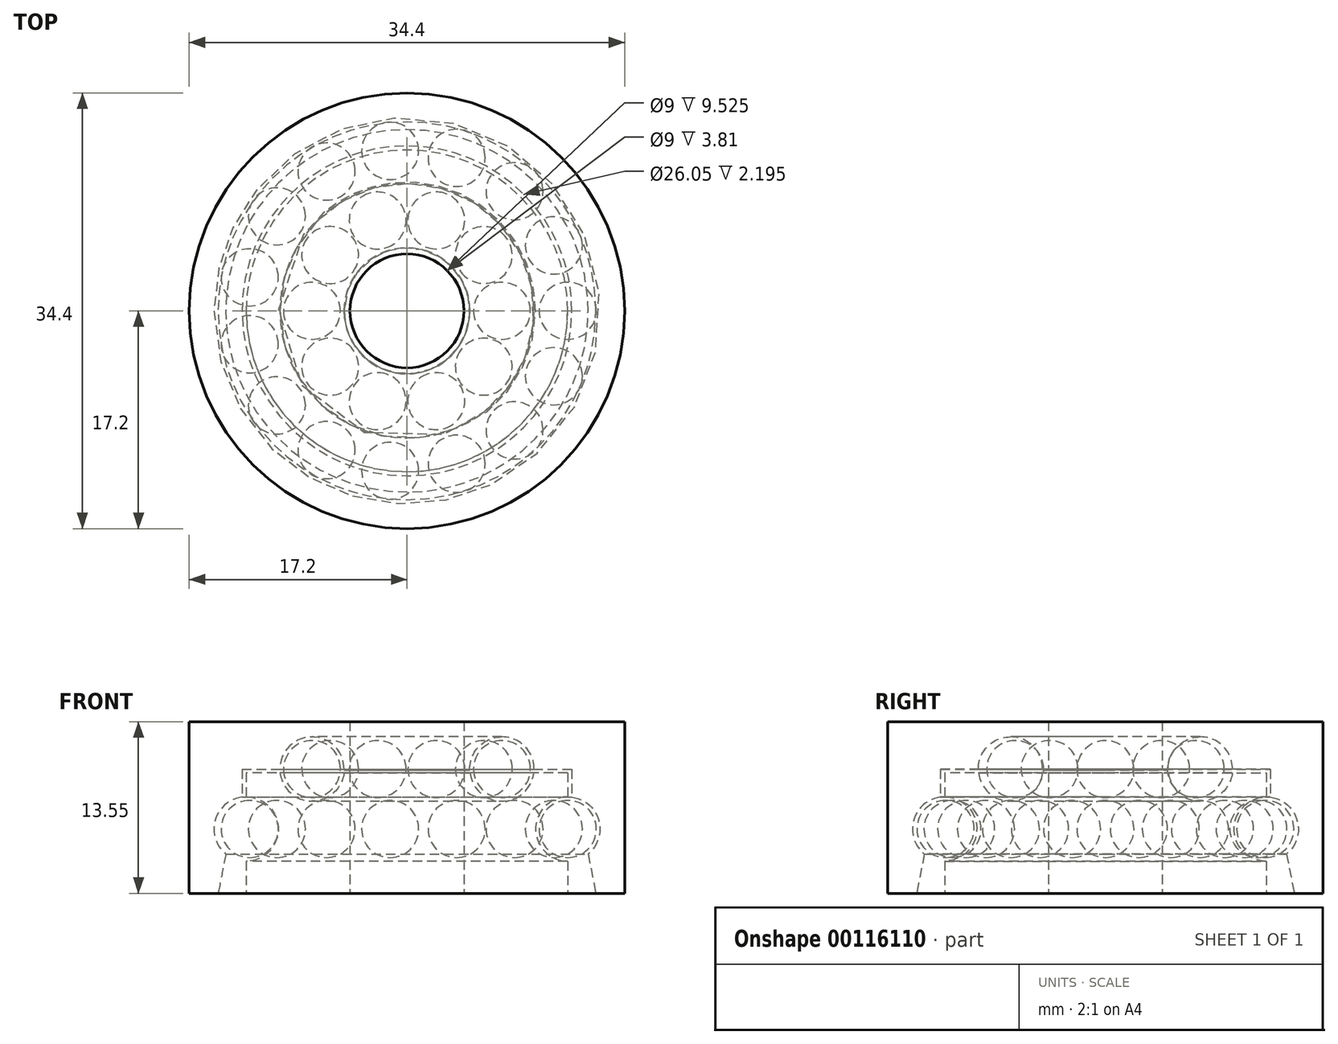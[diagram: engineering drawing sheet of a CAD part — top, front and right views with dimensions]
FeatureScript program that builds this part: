
annotation { "Feature Type Name" : "Feature", "Feature Type Description" : "" }
export const myFeature = defineFeature(function(context is Context, id is Id, definition is map)
    precondition{}
    {
        {
            var Q0;
            Q0=qCreatedBy(makeId("Top.planeOp"),FACE);
            var sketch = newSketch(context, id + "F0", { "sketchPlane" : qUnion([Q0])});
            skCircle(sketch, "E0", {"center": v(0, 0) * mm, "radius": 4.5 * mm});
            skCircle(sketch, "E1", {"center": v(0, 0) * mm, "radius": 12.7 * mm});
            skSolve(sketch);
        }
        {
            var Q0;
            Q0=makeQuery(id+"F0.imprint","IMPRINT",FACE,{"disambiguationData":[TD([[makeQuery(id+"F0.imprint","IMPRINT",EDGE,{"derivedFrom":sQuery(id+"F0.wireOp",EDGE,"E0")}),-1.0]])]});
            extrude(context, id + "F1", {"entities" : qUnion([Q0]), "depth" : 9.52 * mm});
        }
        {
            var Q0;
            Q0=qCreatedBy(makeId("Front.planeOp"),FACE);
            var sketch = newSketch(context, id + "F2", { "sketchPlane" : qUnion([Q0])});
            skCircle(sketch, "E2", {"center": v(7.5, 9.82) * mm, "radius": 2.25 * mm});
            skCircle(sketch, "E3", {"center": v(7.5, 9.82) * mm, "radius": 2.54 * mm});
            skCircle(sketch, "E4", {"center": v(12.7, 5.08) * mm, "radius": 2.26 * mm});
            skCircle(sketch, "E5", {"center": v(12.7, 5.08) * mm, "radius": 2.54 * mm});
            skLineSegment(sketch, "E6", {"start": v(5.25, 9.82) * mm, "end": v(9.75, 9.82) * mm});
            skLineSegment(sketch, "E7", {"start": v(12.7, 7.34) * mm, "end": v(12.7, 2.82) * mm});
            skSolve(sketch);
        }
        {
            var Q0;
            Q0=makeQuery(id+"F2.imprint","IMPRINT",FACE,{"disambiguationData":[TD([[makeQuery(id+"F2.imprint","IMPRINT",EDGE,{"derivedFrom":sQuery(id+"F2.wireOp",EDGE,"E2")}),-1.0]])]});
            var Q1;
            Q1=makeQuery(id+"F2.imprint","IMPRINT",FACE,{"disambiguationData":[TD([[makeQuery(id+"F2.imprint","IMPRINT",EDGE,{"derivedFrom":sQuery(id+"F2.wireOp",EDGE,"E4")}),-1.0]])]});
            var Q2;
            Q2=makeQuery(id+"F2.imprint","IMPRINT",FACE,{"disambiguationData":[TD([[makeQuery(id+"F2.imprint","IMPRINT",EDGE,{"derivedFrom":sQuery(id+"F2.wireOp",EDGE,"E4")}),1.0]])]});
            var Q3;
            Q3=makeQuery(id+"F2.imprint","IMPRINT",FACE,{"disambiguationData":[TD([[makeQuery(id+"F2.imprint","IMPRINT",EDGE,{"derivedFrom":sQuery(id+"F2.wireOp",EDGE,"E2")}),1.0]])]});
            var Q4;
            Q4=makeQuery(id+"F1.opExtrude","CAP_EDGE",EDGE,{"disambiguationData":[OSD([sQuery(id+"F0.wireOp",EDGE,"E0")])],"isStart":false});
            revolve(context, id + "F3", {"operationType" : NewBodyOperationType.REMOVE, "entities" : qUnion([Q0, Q1, Q2, Q3]), "axis" : qUnion([Q4]), "revolveType" : RevolveType.FULL, "oppositeDirection" : true});
        }
        {
            var Q0;
            Q0=qCreatedBy(makeId("Front.planeOp"),FACE);
            var sketch = newSketch(context, id + "F4", { "sketchPlane" : qUnion([Q0])});
            skCircle(sketch, "E8.0", {"center": v(12.7, 5.08) * mm, "radius": 2.54 * mm});
            skCircle(sketch, "E9.0", {"center": v(7.5, 9.82) * mm, "radius": 2.54 * mm});
            skLineSegment(sketch, "E10", {"start": v(4.96, 9.74) * mm, "end": v(4.5, 9.74) * mm});
            skLineSegment(sketch, "E11", {"start": v(4.5, 9.74) * mm, "end": v(4.5, 13.55) * mm});
            skLineSegment(sketch, "E12", {"start": v(4.5, 13.55) * mm, "end": v(17.2, 13.55) * mm});
            skLineSegment(sketch, "E13", {"start": v(17.2, 13.55) * mm, "end": v(17.2, 0) * mm});
            skLineSegment(sketch, "E14", {"start": v(17.2, 0) * mm, "end": v(14.91, 0) * mm});
            skLineSegment(sketch, "E15", {"start": v(14.91, 0) * mm, "end": v(14.3, 3.11) * mm});
            skLineSegment(sketch, "E16", {"start": v(13.03, 7.6) * mm, "end": v(13.03, 9.8) * mm});
            skLineSegment(sketch, "E17", {"start": v(13.03, 9.8) * mm, "end": v(10.04, 9.8) * mm});
            skSolve(sketch);
        }
        {
            var Q0;
            {var subQ0=sQuery(id+"F4.wireOp",EDGE,"E10");Q0=makeQuery(id+"F4.imprint","IMPRINT",FACE,{"disambiguationData":[TD([[makeQuery(id+"F4.imprint","IMPRINT",EDGE,{"derivedFrom":subQ0}),-1.0]])]});}
            var Q1;
            Q1=makeQuery(id+"F1.opExtrude","CAP_EDGE",EDGE,{"disambiguationData":[OSD([sQuery(id+"F0.wireOp",EDGE,"E1")])],"isStart":false});
            revolve(context, id + "F5", {"entities" : qUnion([Q0]), "axis" : qUnion([Q1]), "revolveType" : RevolveType.FULL});
        }
        {
            var Q0;
            {var subQ0=sQuery(id+"F2.wireOp",EDGE,"E6");Q0=makeQuery(id+"F2.imprint","IMPRINT",FACE,{"disambiguationData":[TD([[makeQuery(id+"F2.imprint","IMPRINT",EDGE,{"derivedFrom":subQ0}),1.0]])]});}
            var Q1;
            Q1=sQuery(id+"F2.wireOp",EDGE,"E6");
            revolve(context, id + "F6", {"entities" : qUnion([Q0]), "axis" : qUnion([Q1]), "revolveType" : RevolveType.FULL});
        }
        {
            var Q0;
            {var subQ0=sQuery(id+"F2.wireOp",EDGE,"E7");Q0=makeQuery(id+"F2.imprint","IMPRINT",FACE,{"disambiguationData":[TD([[makeQuery(id+"F2.imprint","IMPRINT",EDGE,{"derivedFrom":subQ0}),1.0]])]});}
            var Q1;
            Q1=sQuery(id+"F2.wireOp",EDGE,"E7");
            revolve(context, id + "F7", {"entities" : qUnion([Q0]), "axis" : qUnion([Q1]), "revolveType" : RevolveType.FULL});
        }
        {
            var Q0;
            Q0=makeQuery(id+"F6.opRevolve","SWEPT_BODY",BODY,{"disambiguationData":[OSD([sQuery(id+"F2.wireOp",EDGE,"E2"),sQuery(id+"F2.wireOp",EDGE,"E6")])]});
            var Q1;
            Q1=makeQuery(id+"F3.boolean.opBoolean","INTERSECT",EDGE,{"disambiguationData":[OD(0.0)],"derivedFrom":[makeQuery(id+"F1.opExtrude","CAP_FACE",FACE,{"disambiguationData":[OSD([sQuery(id+"F0.wireOp",EDGE,"E0"),sQuery(id+"F0.wireOp",EDGE,"E1")])],"isStart":false}),makeQuery(id+"F3.opRevolve","SWEPT_FACE",FACE,{"disambiguationData":[OSD([sQuery(id+"F2.wireOp",EDGE,"E3")])]})]});
            circularPattern(context, id + "F8", {"entities" : qUnion([Q0]), "axis" : qUnion([Q1]), "angle" : 36 * degree, "instanceCount" : 10});
        }
        {
            var Q0;
            Q0=makeQuery(id+"F7.opRevolve","SWEPT_BODY",BODY,{"disambiguationData":[OSD([sQuery(id+"F2.wireOp",EDGE,"E4"),sQuery(id+"F2.wireOp",EDGE,"E7")])]});
            var Q1;
            Q1=makeQuery(id+"F1.opExtrude","CAP_EDGE",EDGE,{"disambiguationData":[OSD([sQuery(id+"F0.wireOp",EDGE,"E1")])],"isStart":false});
            circularPattern(context, id + "F9", {"entities" : qUnion([Q0]), "axis" : qUnion([Q1]), "angle" : 24 * degree, "instanceCount" : 15});
        }
    });
